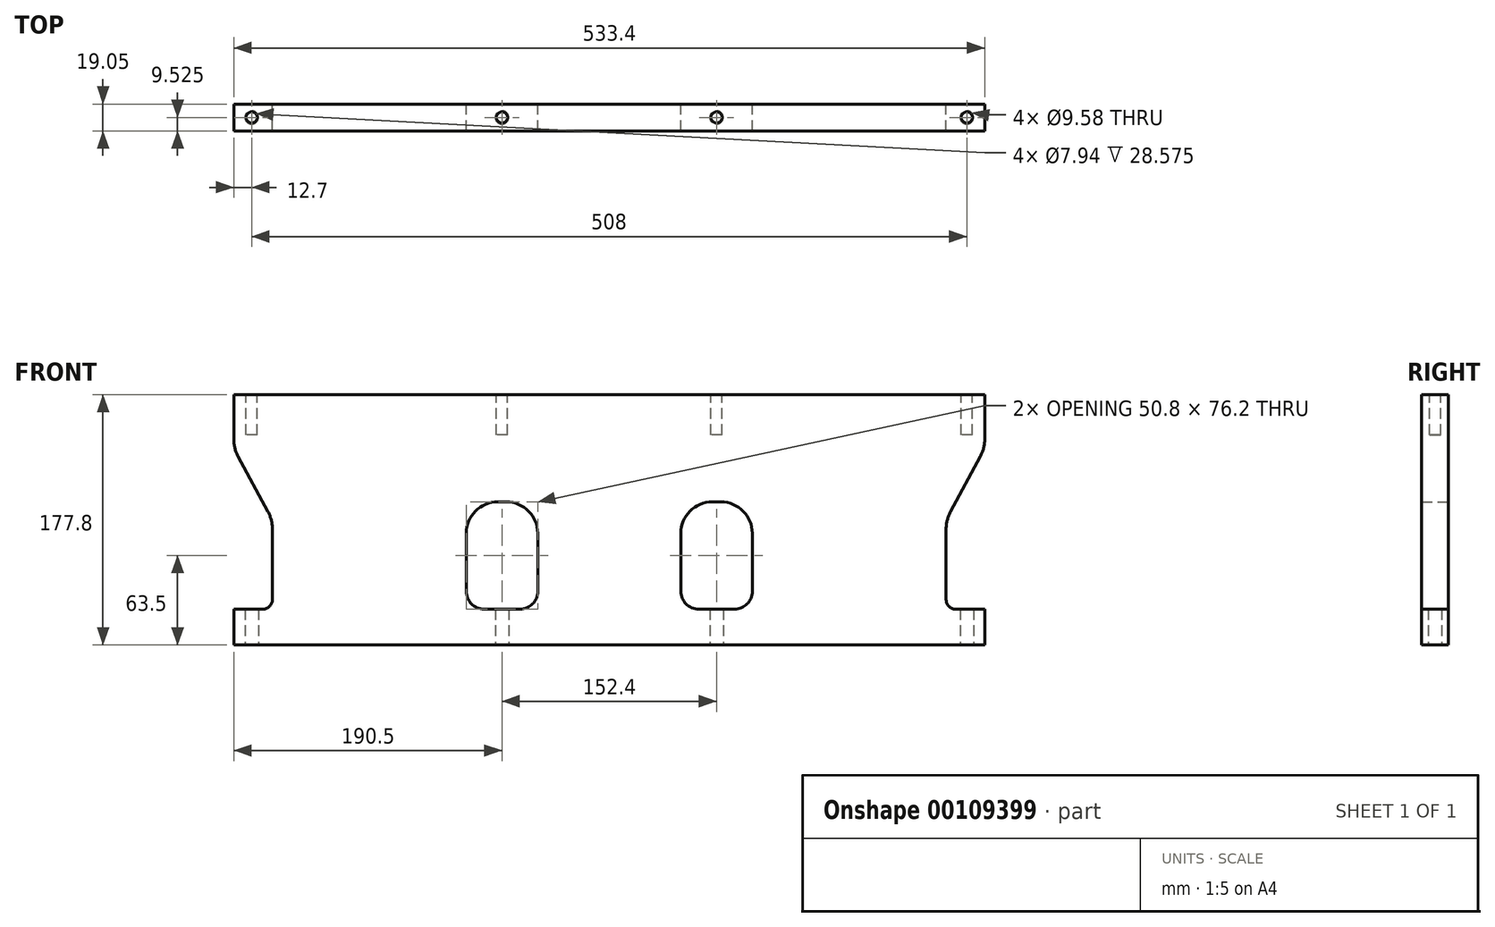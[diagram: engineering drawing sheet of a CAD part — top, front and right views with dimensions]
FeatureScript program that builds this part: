
annotation { "Feature Type Name" : "Feature", "Feature Type Description" : "" }
export const myFeature = defineFeature(function(context is Context, id is Id, definition is map)
    precondition{}
    {
        {
            var Q0;
            Q0=qCreatedBy(makeId("Front.planeOp"),FACE);
            var sketch = newSketch(context, id + "F0", { "sketchPlane" : qUnion([Q0])});
            skLineSegment(sketch, "E0", {"start": v(-266.7, -88.9) * mm, "end": v(-266.7, -63.5) * mm});
            skLineSegment(sketch, "E1", {"start": v(-266.7, -63.5) * mm, "end": v(-245.92, -63.5) * mm});
            skLineSegment(sketch, "E2", {"start": v(-239.32, -56.9) * mm, "end": v(-239.32, 0) * mm});
            skLineSegment(sketch, "E3", {"start": v(-266.7, 88.9) * mm, "end": v(266.7, 88.9) * mm});
            skLineSegment(sketch, "E4", {"start": v(239.32, 0) * mm, "end": v(239.32, -56.9) * mm});
            skLineSegment(sketch, "E5", {"start": v(245.92, -63.5) * mm, "end": v(266.7, -63.5) * mm});
            skLineSegment(sketch, "E6", {"start": v(266.7, -63.5) * mm, "end": v(266.7, -88.9) * mm});
            skLineSegment(sketch, "E7", {"start": v(266.7, -88.9) * mm, "end": v(-266.7, -88.9) * mm});
            skLineSegment(sketch, "E8", {"start": v(0, 88.9) * mm, "end": v(0, -88.9) * mm, "construction": true});
            skLineSegment(sketch, "E9.bottom", {"start": v(-88.9, -63.5) * mm, "end": v(-63.5, -63.5) * mm});
            skLineSegment(sketch, "E9.top", {"start": v(-79.38, 12.7) * mm, "end": v(-73.03, 12.7) * mm});
            skLineSegment(sketch, "E9.left", {"start": v(-101.6, -50.8) * mm, "end": v(-101.6, -9.53) * mm});
            skLineSegment(sketch, "E9.right", {"start": v(-50.8, -50.8) * mm, "end": v(-50.8, -9.52) * mm});
            skPoint(sketch, "E9.middle", {"position": v(-76.2, -25.4) * mm});
            skPoint(sketch, "E10.visualSharp", {"position": v(-101.6, -63.5) * mm});
            skArc(sketch, "E10.filletArc", {"start": v(-101.6, -50.8) * mm, "mid": v(-97.88, -59.78) * mm, "end": v(-88.9, -63.5) * mm});
            skPoint(sketch, "E11.visualSharp", {"position": v(-50.8, -63.5) * mm});
            skArc(sketch, "E11.filletArc", {"start": v(-63.5, -63.5) * mm, "mid": v(-54.52, -59.78) * mm, "end": v(-50.8, -50.8) * mm});
            skPoint(sketch, "E12.visualSharp", {"position": v(-50.8, 12.7) * mm});
            skArc(sketch, "E12.filletArc", {"start": v(-50.8, -9.52) * mm, "mid": v(-57.3, 6.2) * mm, "end": v(-73.03, 12.7) * mm});
            skPoint(sketch, "E13.visualSharp", {"position": v(-101.6, 12.7) * mm});
            skArc(sketch, "E13.filletArc", {"start": v(-79.38, 12.7) * mm, "mid": v(-95.1, 6.2) * mm, "end": v(-101.6, -9.53) * mm});
            skLineSegment(sketch, "E14.MirrorCS", {"start": v(50.8, -50.8) * mm, "end": v(50.8, -9.52) * mm});
            skArc(sketch, "E15.MirrorCS", {"start": v(50.8, -9.52) * mm, "mid": v(57.3, 6.2) * mm, "end": v(73.02, 12.7) * mm});
            skLineSegment(sketch, "E16.MirrorCS", {"start": v(79.37, 12.7) * mm, "end": v(73.02, 12.7) * mm});
            skArc(sketch, "E17.MirrorCS", {"start": v(79.37, 12.7) * mm, "mid": v(95.1, 6.2) * mm, "end": v(101.6, -9.52) * mm});
            skLineSegment(sketch, "E18.MirrorCS", {"start": v(101.6, -50.8) * mm, "end": v(101.6, -9.52) * mm});
            skArc(sketch, "E19.MirrorCS", {"start": v(101.6, -50.8) * mm, "mid": v(97.88, -59.78) * mm, "end": v(88.9, -63.5) * mm});
            skLineSegment(sketch, "E20.MirrorCS", {"start": v(88.9, -63.5) * mm, "end": v(63.5, -63.5) * mm});
            skArc(sketch, "E21.MirrorCS", {"start": v(63.5, -63.5) * mm, "mid": v(54.52, -59.78) * mm, "end": v(50.8, -50.8) * mm});
            skPoint(sketch, "E22.visualSharp", {"position": v(-239.32, -63.5) * mm});
            skArc(sketch, "E22.filletArc", {"start": v(-245.92, -63.5) * mm, "mid": v(-241.25, -61.57) * mm, "end": v(-239.32, -56.9) * mm});
            skPoint(sketch, "E23.visualSharp", {"position": v(239.32, -63.5) * mm});
            skArc(sketch, "E23.filletArc", {"start": v(239.32, -56.9) * mm, "mid": v(241.25, -61.57) * mm, "end": v(245.92, -63.5) * mm});
            skPoint(sketch, "E24.visualSharp", {"position": v(-239.32, 63.5) * mm});
            skLineSegment(sketch, "E25", {"start": v(-266.7, 88.9) * mm, "end": v(-266.7, 50.8) * mm});
            skLineSegment(sketch, "E26", {"start": v(266.7, 88.9) * mm, "end": v(266.7, 50.8) * mm});
            skLineSegment(sketch, "E27", {"start": v(-266.7, 50.8) * mm, "end": v(-239.32, 0) * mm});
            skLineSegment(sketch, "E28", {"start": v(266.7, 50.8) * mm, "end": v(239.32, 0) * mm});
            skSolve(sketch);
        }
        {
            var Q0;
            Q0 = qSketchRegion(id + "F0", true);
            extrude(context, id + "F1", {"entities" : qUnion([Q0]), "depth" : 19.05 * mm});
        }
        {
            var Q0;
            Q0=makeQuery(id+"F1.opExtrude","SWEPT_EDGE",EDGE,{"disambiguationData":[OSD([sQuery(id+"F0.wireOp",EDGE,"DLczSlfx-CuRs-rcjQ-uIHg-AwoYi9h0VctZ"),sQuery(id+"F0.wireOp",EDGE,"E24.filletArc")])]});
            var Q1;
            Q1=makeQuery(id+"F1.opExtrude","SWEPT_EDGE",EDGE,{"disambiguationData":[OSD([sQuery(id+"F0.wireOp",EDGE,"Q2dkD7ng-ADv0-cFVC-gkPA-OT77blCQegdU"),sQuery(id+"F0.wireOp",EDGE,"483fbb43-eb60-49ff-a213-be12c32937cf.filletArc")])]});
            var Q2;
            Q2=makeQuery(id+"F1.opExtrude","SWEPT_EDGE",EDGE,{"disambiguationData":[OSD([sQuery(id+"F0.wireOp",EDGE,"E25"),sQuery(id+"F0.wireOp",EDGE,"E27")])]});
            var Q3;
            Q3=makeQuery(id+"F1.opExtrude","SWEPT_EDGE",EDGE,{"disambiguationData":[OSD([sQuery(id+"F0.wireOp",EDGE,"E2"),sQuery(id+"F0.wireOp",EDGE,"E27")])]});
            var Q4;
            Q4=makeQuery(id+"F1.opExtrude","SWEPT_EDGE",EDGE,{"disambiguationData":[OSD([sQuery(id+"F0.wireOp",EDGE,"E26"),sQuery(id+"F0.wireOp",EDGE,"E28")])]});
            var Q5;
            Q5=makeQuery(id+"F1.opExtrude","SWEPT_EDGE",EDGE,{"disambiguationData":[OSD([sQuery(id+"F0.wireOp",EDGE,"E4"),sQuery(id+"F0.wireOp",EDGE,"E28")])]});
            fillet(context, id + "F2", {"entities" : qUnion([Q0, Q1, Q2, Q3, Q4, Q5]), "radius" : 25.4 * mm, "tangentPropagation" : true, "allowEdgeOverflow" : false});
        }
        {
            var Q0;
            Q0=makeQuery(id+"F1.opExtrude","SWEPT_FACE",FACE,{"disambiguationData":[OSD([sQuery(id+"F0.wireOp",EDGE,"E7")])]});
            var sketch = newSketch(context, id + "F3", { "sketchPlane" : qUnion([Q0])});
            skCircle(sketch, "E29", {"center": v(-254, 9.53) * mm, "radius": 4.79 * mm});
            skCircle(sketch, "E30", {"center": v(-76.2, 9.53) * mm, "radius": 4.79 * mm});
            skLineSegment(sketch, "E31", {"start": v(-266.7, 9.53) * mm, "end": v(-254, 9.53) * mm, "construction": true});
            skLineSegment(sketch, "E32", {"start": v(0, 0) * mm, "end": v(0, 19.05) * mm, "construction": true});
            skCircle(sketch, "E33.MirrorC", {"center": v(254, 9.53) * mm, "radius": 4.79 * mm});
            skCircle(sketch, "E34.MirrorC", {"center": v(76.2, 9.53) * mm, "radius": 4.79 * mm});
            skCircle(sketch, "E35", {"center": v(-254, 9.53) * mm, "radius": 7.14 * mm, "construction": true});
            skSolve(sketch);
        }
        {
            var Q0;
            Q0 = qSketchRegion(id + "F3", true);
            extrude(context, id + "F4", {"entities" : qUnion([Q0]), "operationType" : NewBodyOperationType.REMOVE, "oppositeDirection" : true, "depth" : 33.02 * mm});
        }
        {
            var Q0;
            Q0=makeQuery(id+"F1.opExtrude","SWEPT_FACE",FACE,{"disambiguationData":[OSD([sQuery(id+"F0.wireOp",EDGE,"E3")])]});
            var sketch = newSketch(context, id + "F5", { "sketchPlane" : qUnion([Q0])});
            skCircle(sketch, "E36", {"center": v(-254, -9.53) * mm, "radius": 3.97 * mm});
            skCircle(sketch, "E37", {"center": v(-76.2, -9.53) * mm, "radius": 3.97 * mm});
            skCircle(sketch, "E38", {"center": v(76.2, -9.53) * mm, "radius": 3.97 * mm});
            skCircle(sketch, "E39", {"center": v(254, -9.53) * mm, "radius": 3.97 * mm});
            skSolve(sketch);
        }
        {
            var Q0;
            Q0 = qSketchRegion(id + "F5", true);
            extrude(context, id + "F6", {"entities" : qUnion([Q0]), "operationType" : NewBodyOperationType.REMOVE, "oppositeDirection" : true, "depth" : 28.57 * mm});
        }
    });
